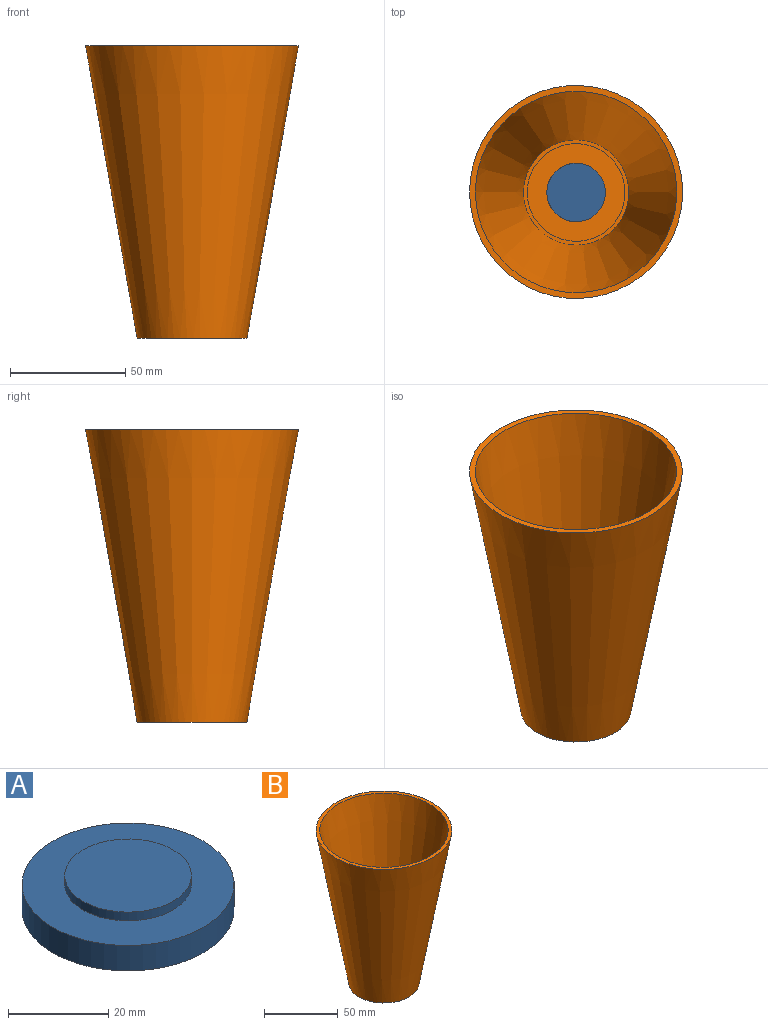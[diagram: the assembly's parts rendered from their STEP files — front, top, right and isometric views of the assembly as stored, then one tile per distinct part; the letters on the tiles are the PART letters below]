
ASSEMBLY  parts=2 mates=1
PART A: 11 faces, bbox 42.4x42.4x8.4 mm
  f0: plane 42.42x42.42mm, normal (0,0,-1), area 1157.5mm2, adj f4,f5,f6,f8,f9
  f1: plane 25.35x25.35mm, normal (0,0,1), area 504.7mm2, adj f2
  f2: cylinder r=12.67mm len=25.35mm, axis (0,0,1), area 169.9mm2, adj f1,f3
  f3: plane 42.42x42.42mm, normal (0,0,1), area 908.5mm2, adj f2,f4
  f4: cylinder r=21.21mm len=42.42mm, axis (0,0,1), area 829.3mm2, adj f0,f3
  f5: plane 23.28x1.27mm, normal (0,-1,0), area 29.6mm2, adj f0,f6,f7
  f6: cylinder r=12.7mm len=23.28mm, axis (0,0,-1), area 37.4mm2, adj f0,f5,f7
  f7: plane 23.28x7.62mm, normal (0,0,-1), area 127.9mm2, adj f5,f6
  f8: plane 23.28x1.27mm, normal (0,1,0), area 29.6mm2, adj f0,f9,f10
  f9: cylinder r=12.7mm len=23.28mm, axis (0,0,-1), area 37.4mm2, adj f0,f8,f10
  f10: plane 23.28x7.62mm, normal (0,0,-1), area 127.9mm2, adj f8,f9
PART B: 9 faces, bbox 92.5x92.5x127 mm
  f0: cylinder r=12.7mm len=25.4mm, axis (0,0,-1), area 172.3mm2, adj f1,f8
  f1: plane 25.4x25.4mm, normal (0,0,-1), area 506.7mm2, adj f0
  f2: plane 45.72x45.72mm, normal (0,0,1), area 1641.7mm2, adj f3
  f3: cone r=43.69mm half-angle=10deg, axis (0,0,1), area 25073mm2, adj f2,f4
  f4: plane 92.45x92.45mm, normal (0,0,1), area 717.5mm2, adj f3,f5
  f5: cone r=46.23mm half-angle=10deg, axis (0,0,1), area 28383.3mm2, adj f4,f6
  f6: plane 47.67x47.67mm, normal (0,0,-1), area 360.1mm2, adj f5,f7
  f7: cylinder r=21.29mm len=42.59mm, axis (0,0,-1), area 849.5mm2, adj f6,f8
  f8: plane 42.59x42.59mm, normal (0,0,-1), area 917.6mm2, adj f0,f7
PLACE A t=(-2.92,-2.17,-34.08)mm
PLACE B t=(-2.92,-2.17,-2.97)mm
MATE revolute B.f0 <-> A.f2  axis (0,0,-1) through (-2.92,-2.17,-43.72)mm
